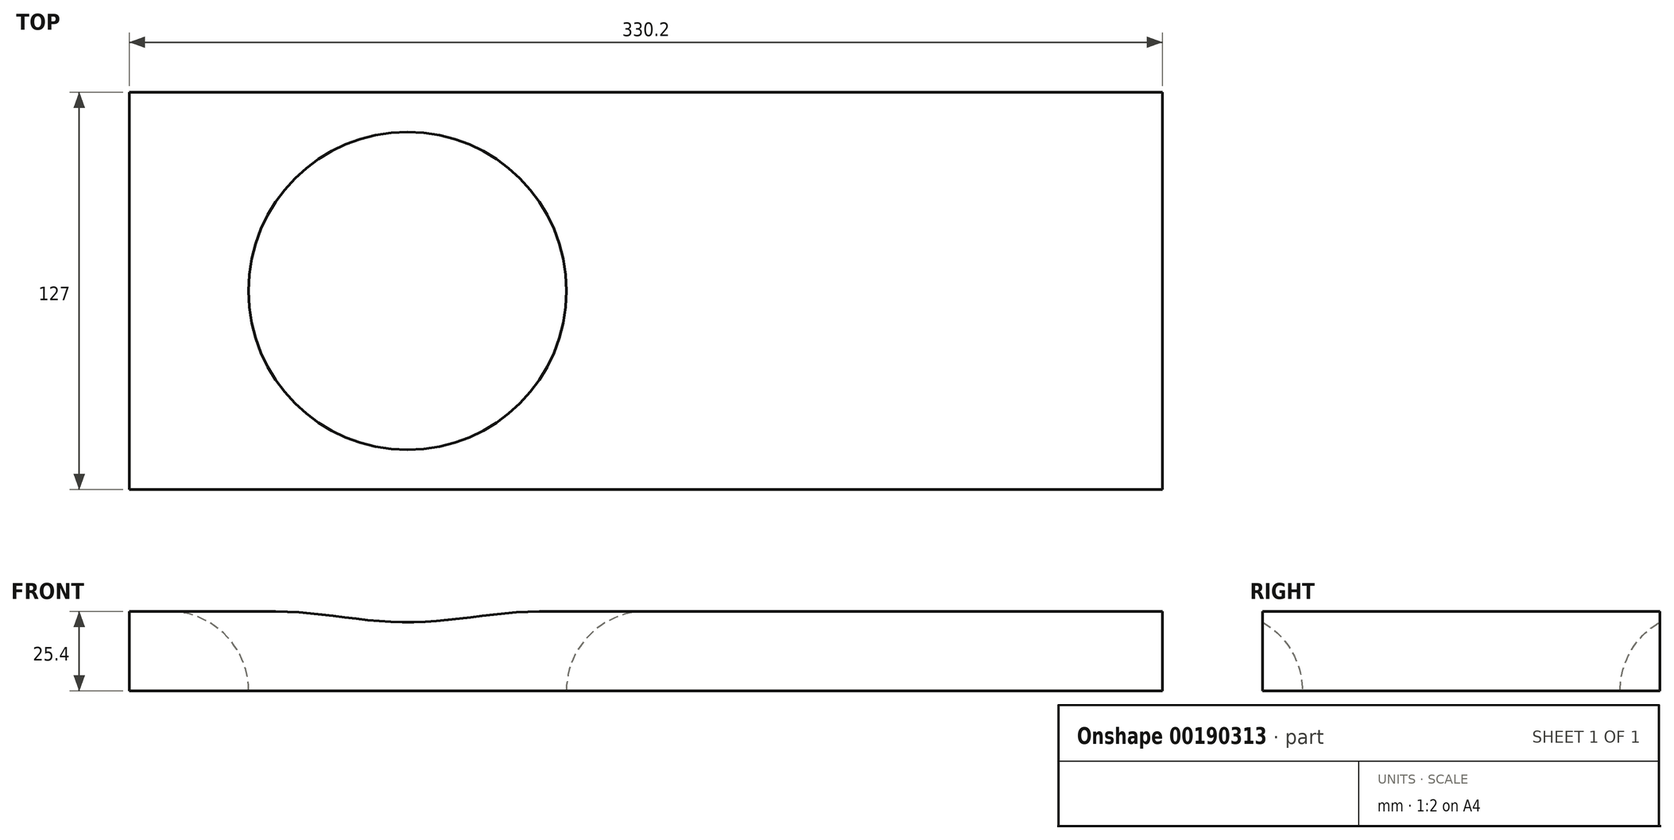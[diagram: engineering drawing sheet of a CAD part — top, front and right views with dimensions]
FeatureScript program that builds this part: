
annotation { "Feature Type Name" : "Feature", "Feature Type Description" : "" }
export const myFeature = defineFeature(function(context is Context, id is Id, definition is map)
    precondition{}
    {
        {
            var Q0;
            Q0=qCreatedBy(makeId("Top.planeOp"),FACE);
            var sketch = newSketch(context, id + "F0", { "sketchPlane" : qUnion([Q0])});
            skLineSegment(sketch, "E0.bottom", {"start": v(-165.1, 63.5) * mm, "end": v(165.1, 63.5) * mm});
            skLineSegment(sketch, "E0.top", {"start": v(-165.1, -63.5) * mm, "end": v(165.1, -63.5) * mm});
            skLineSegment(sketch, "E0.left", {"start": v(-165.1, 63.5) * mm, "end": v(-165.1, -63.5) * mm});
            skLineSegment(sketch, "E0.right", {"start": v(165.1, 63.5) * mm, "end": v(165.1, -63.5) * mm});
            skPoint(sketch, "E0.middle", {"position": v(0, 0) * mm});
            skLineSegment(sketch, "E1", {"start": v(-165.1, 0) * mm, "end": v(165.1, 0) * mm, "construction": true});
            skCircle(sketch, "E2", {"center": v(-76.2, 0) * mm, "radius": 50.8 * mm});
            skSolve(sketch);
        }
        {
            var Q0;
            Q0 = qSketchRegion(id + "F0", true);
            extrude(context, id + "F1", {"entities" : qUnion([Q0]), "depth" : 25.4 * mm});
        }
        {
            var Q0;
            Q0=makeQuery(id+"F1.opExtrude","CAP_EDGE",EDGE,{"disambiguationData":[OSD([sQuery(id+"F0.wireOp",EDGE,"E2")])],"isStart":false});
            fillet(context, id + "F2", {"entities" : qUnion([Q0]), "radius" : 25.4 * mm, "tangentPropagation" : true, "allowEdgeOverflow" : false});
        }
    });
